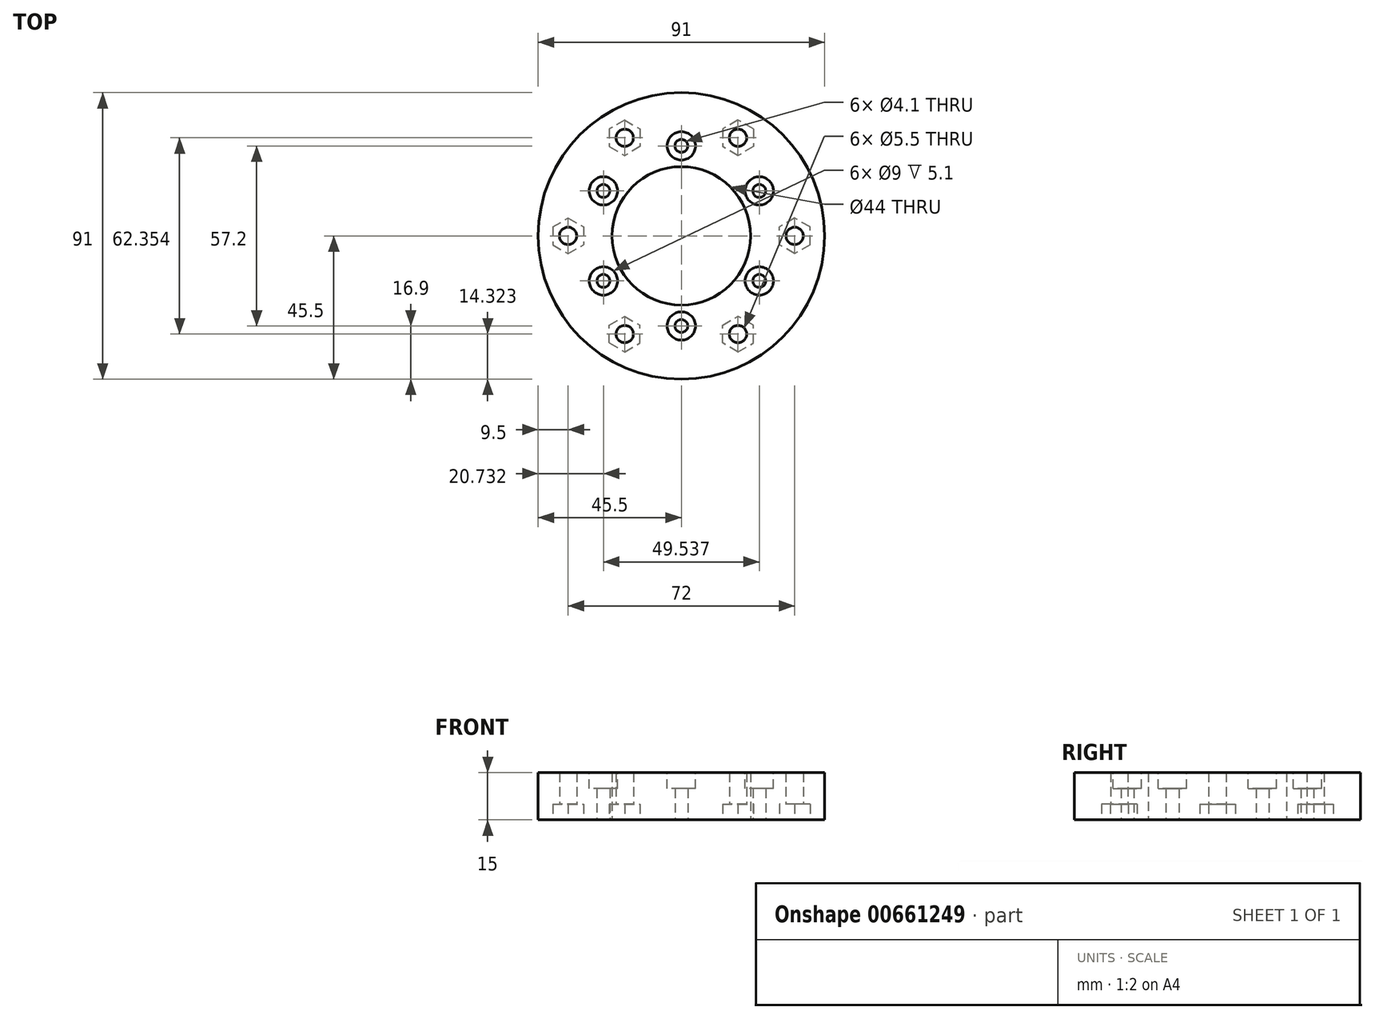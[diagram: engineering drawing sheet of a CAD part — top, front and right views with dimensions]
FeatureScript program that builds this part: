
annotation { "Feature Type Name" : "Feature", "Feature Type Description" : "" }
export const myFeature = defineFeature(function(context is Context, id is Id, definition is map)
    precondition{}
    {
        {
            var Q0;
            Q0=qCreatedBy(makeId("Top.planeOp"),FACE);
            var sketch = newSketch(context, id + "F0", { "sketchPlane" : qUnion([Q0])});
            skCircle(sketch, "E0", {"center": v(0, 0) * mm, "radius": 36 * mm, "construction": true});
            skCircle(sketch, "E1", {"center": v(18, 31.18) * mm, "radius": 2.75 * mm});
            skCircle(sketch, "E2", {"center": v(36, 0) * mm, "radius": 2.75 * mm});
            skCircle(sketch, "E3", {"center": v(-18, 31.18) * mm, "radius": 2.75 * mm});
            skCircle(sketch, "E4", {"center": v(-36, 0) * mm, "radius": 2.75 * mm});
            skCircle(sketch, "E5", {"center": v(-18, -31.18) * mm, "radius": 2.75 * mm});
            skCircle(sketch, "E6", {"center": v(18, -31.18) * mm, "radius": 2.75 * mm});
            skCircle(sketch, "E7", {"center": v(0, 0) * mm, "radius": 45.5 * mm});
            skCircle(sketch, "E8", {"center": v(0, 0) * mm, "radius": 28.6 * mm, "construction": true});
            skCircle(sketch, "E9", {"center": v(0, 28.6) * mm, "radius": 2.05 * mm});
            skCircle(sketch, "E10", {"center": v(24.77, 14.3) * mm, "radius": 2.05 * mm});
            skCircle(sketch, "E11", {"center": v(24.77, -14.3) * mm, "radius": 2.05 * mm});
            skCircle(sketch, "E12", {"center": v(0, -28.6) * mm, "radius": 2.05 * mm});
            skCircle(sketch, "E13", {"center": v(-24.77, -14.3) * mm, "radius": 2.05 * mm});
            skCircle(sketch, "E14", {"center": v(-24.77, 14.3) * mm, "radius": 2.05 * mm});
            skCircle(sketch, "E15", {"center": v(0, 0) * mm, "radius": 22 * mm});
            skCircle(sketch, "E16", {"center": v(-18, -31.18) * mm, "radius": 5.65 * mm, "construction": true});
            skLineSegment(sketch, "E17", {"start": v(-18, -31.18) * mm, "end": v(-18, -25.53) * mm, "construction": true});
            skLineSegment(sketch, "E18", {"start": v(-18, -25.53) * mm, "end": v(-13.1, -28.35) * mm});
            skLineSegment(sketch, "E19", {"start": v(-13.1, -28.35) * mm, "end": v(-18, -31.18) * mm, "construction": true});
            skLineSegment(sketch, "E20", {"start": v(-18, -31.18) * mm, "end": v(-13.1, -34) * mm, "construction": true});
            skLineSegment(sketch, "E21", {"start": v(-13.1, -34) * mm, "end": v(-13.1, -28.35) * mm});
            skLineSegment(sketch, "E22", {"start": v(-18, -31.18) * mm, "end": v(-18, -36.83) * mm, "construction": true});
            skLineSegment(sketch, "E23", {"start": v(-18, -36.83) * mm, "end": v(-13.1, -34) * mm});
            skLineSegment(sketch, "E24", {"start": v(-18, -31.18) * mm, "end": v(-22.9, -34) * mm, "construction": true});
            skLineSegment(sketch, "E25", {"start": v(-22.9, -34) * mm, "end": v(-18, -36.83) * mm});
            skLineSegment(sketch, "E26", {"start": v(-22.9, -34) * mm, "end": v(-22.9, -28.35) * mm});
            skLineSegment(sketch, "E27", {"start": v(-22.9, -28.35) * mm, "end": v(-18, -31.18) * mm, "construction": true});
            skLineSegment(sketch, "E28", {"start": v(-22.9, -28.35) * mm, "end": v(-18, -25.53) * mm});
            skLineSegment(sketch, "E29.1.0", {"start": v(13.1, -28.35) * mm, "end": v(18, -25.53) * mm});
            skLineSegment(sketch, "E29.1.1", {"start": v(22.9, -28.35) * mm, "end": v(18, -25.53) * mm});
            skLineSegment(sketch, "E29.1.2", {"start": v(22.9, -34) * mm, "end": v(22.9, -28.35) * mm});
            skLineSegment(sketch, "E29.1.3", {"start": v(18, -36.83) * mm, "end": v(22.9, -34) * mm});
            skLineSegment(sketch, "E29.1.4", {"start": v(18, -36.83) * mm, "end": v(13.1, -34) * mm});
            skLineSegment(sketch, "E29.1.5", {"start": v(13.1, -34) * mm, "end": v(13.1, -28.35) * mm});
            skLineSegment(sketch, "E29.2.0", {"start": v(31.1, -2.82) * mm, "end": v(31.1, 2.83) * mm});
            skLineSegment(sketch, "E29.2.1", {"start": v(36, 5.65) * mm, "end": v(31.1, 2.83) * mm});
            skLineSegment(sketch, "E29.2.2", {"start": v(40.9, 2.83) * mm, "end": v(36, 5.65) * mm});
            skLineSegment(sketch, "E29.2.3", {"start": v(40.9, -2.82) * mm, "end": v(40.9, 2.83) * mm});
            skLineSegment(sketch, "E29.2.4", {"start": v(40.9, -2.82) * mm, "end": v(36, -5.65) * mm});
            skLineSegment(sketch, "E29.2.5", {"start": v(36, -5.65) * mm, "end": v(31.1, -2.82) * mm});
            skLineSegment(sketch, "E29.3.0", {"start": v(18, 25.53) * mm, "end": v(13.1, 28.35) * mm});
            skLineSegment(sketch, "E29.3.1", {"start": v(13.1, 34) * mm, "end": v(13.1, 28.35) * mm});
            skLineSegment(sketch, "E29.3.2", {"start": v(18, 36.83) * mm, "end": v(13.1, 34) * mm});
            skLineSegment(sketch, "E29.3.3", {"start": v(22.9, 34) * mm, "end": v(18, 36.83) * mm});
            skLineSegment(sketch, "E29.3.4", {"start": v(22.9, 34) * mm, "end": v(22.9, 28.35) * mm});
            skLineSegment(sketch, "E29.3.5", {"start": v(22.9, 28.35) * mm, "end": v(18, 25.53) * mm});
            skLineSegment(sketch, "E29.4.0", {"start": v(-13.1, 28.35) * mm, "end": v(-18, 25.53) * mm});
            skLineSegment(sketch, "E29.4.1", {"start": v(-22.9, 28.35) * mm, "end": v(-18, 25.53) * mm});
            skLineSegment(sketch, "E29.4.2", {"start": v(-22.9, 34) * mm, "end": v(-22.9, 28.35) * mm});
            skLineSegment(sketch, "E29.4.3", {"start": v(-18, 36.83) * mm, "end": v(-22.9, 34) * mm});
            skLineSegment(sketch, "E29.4.4", {"start": v(-18, 36.83) * mm, "end": v(-13.1, 34) * mm});
            skLineSegment(sketch, "E29.4.5", {"start": v(-13.1, 34) * mm, "end": v(-13.1, 28.35) * mm});
            skLineSegment(sketch, "E29.5.0", {"start": v(-31.1, 2.82) * mm, "end": v(-31.1, -2.83) * mm});
            skLineSegment(sketch, "E29.5.1", {"start": v(-36, -5.65) * mm, "end": v(-31.1, -2.83) * mm});
            skLineSegment(sketch, "E29.5.2", {"start": v(-40.9, -2.83) * mm, "end": v(-36, -5.65) * mm});
            skLineSegment(sketch, "E29.5.3", {"start": v(-40.9, 2.82) * mm, "end": v(-40.9, -2.83) * mm});
            skLineSegment(sketch, "E29.5.4", {"start": v(-40.9, 2.82) * mm, "end": v(-36, 5.65) * mm});
            skLineSegment(sketch, "E29.5.5", {"start": v(-36, 5.65) * mm, "end": v(-31.1, 2.82) * mm});
            skSolve(sketch);
        }
        {
            var Q0;
            Q0=makeQuery(id+"F0.imprint","IMPRINT",FACE,{"disambiguationData":[TD([[makeQuery(id+"F0.imprint","IMPRINT",EDGE,{"derivedFrom":sQuery(id+"F0.wireOp",EDGE,"E7")}),1.0]])]});
            var Q1;
            Q1=makeQuery(id+"F0.imprint","IMPRINT",FACE,{"disambiguationData":[TD([[makeQuery(id+"F0.imprint","IMPRINT",EDGE,{"derivedFrom":sQuery(id+"F0.wireOp",EDGE,"E4")}),-1.0]])]});
            var Q2;
            Q2=makeQuery(id+"F0.imprint","IMPRINT",FACE,{"disambiguationData":[TD([[makeQuery(id+"F0.imprint","IMPRINT",EDGE,{"derivedFrom":sQuery(id+"F0.wireOp",EDGE,"E5")}),-1.0]])]});
            var Q3;
            Q3=makeQuery(id+"F0.imprint","IMPRINT",FACE,{"disambiguationData":[TD([[makeQuery(id+"F0.imprint","IMPRINT",EDGE,{"derivedFrom":sQuery(id+"F0.wireOp",EDGE,"E6")}),-1.0]])]});
            var Q4;
            Q4=makeQuery(id+"F0.imprint","IMPRINT",FACE,{"disambiguationData":[TD([[makeQuery(id+"F0.imprint","IMPRINT",EDGE,{"derivedFrom":sQuery(id+"F0.wireOp",EDGE,"E2")}),-1.0]])]});
            var Q5;
            Q5=makeQuery(id+"F0.imprint","IMPRINT",FACE,{"disambiguationData":[TD([[makeQuery(id+"F0.imprint","IMPRINT",EDGE,{"derivedFrom":sQuery(id+"F0.wireOp",EDGE,"E1")}),-1.0]])]});
            var Q6;
            Q6=makeQuery(id+"F0.imprint","IMPRINT",FACE,{"disambiguationData":[TD([[makeQuery(id+"F0.imprint","IMPRINT",EDGE,{"derivedFrom":sQuery(id+"F0.wireOp",EDGE,"E3")}),-1.0]])]});
            extrude(context, id + "F1", {"entities" : qUnion([Q0, Q1, Q2, Q3, Q4, Q5, Q6]), "depth" : 15 * mm, "offsetDistance" : 25 * mm});
        }
        {
            var Q0;
            Q0=makeQuery(id+"F1.opExtrude","CAP_FACE",FACE,{"disambiguationData":[OSD([sQuery(id+"F0.wireOp",EDGE,"E1"),sQuery(id+"F0.wireOp",EDGE,"E2"),sQuery(id+"F0.wireOp",EDGE,"E3"),sQuery(id+"F0.wireOp",EDGE,"E4"),sQuery(id+"F0.wireOp",EDGE,"E5"),sQuery(id+"F0.wireOp",EDGE,"E6"),sQuery(id+"F0.wireOp",EDGE,"E7"),sQuery(id+"F0.wireOp",EDGE,"E9"),sQuery(id+"F0.wireOp",EDGE,"E10"),sQuery(id+"F0.wireOp",EDGE,"E11"),sQuery(id+"F0.wireOp",EDGE,"E12"),sQuery(id+"F0.wireOp",EDGE,"E13"),sQuery(id+"F0.wireOp",EDGE,"E14"),sQuery(id+"F0.wireOp",EDGE,"E15")])],"isStart":false});
            var sketch = newSketch(context, id + "F2", { "sketchPlane" : qUnion([Q0])});
            skCircle(sketch, "E30", {"center": v(-24.77, -14.3) * mm, "radius": 4.5 * mm});
            skCircle(sketch, "E31", {"center": v(-24.77, 14.3) * mm, "radius": 4.5 * mm});
            skCircle(sketch, "E32", {"center": v(0, 28.6) * mm, "radius": 4.5 * mm});
            skCircle(sketch, "E33", {"center": v(24.77, 14.3) * mm, "radius": 4.5 * mm});
            skCircle(sketch, "E34", {"center": v(24.77, -14.3) * mm, "radius": 4.5 * mm});
            skCircle(sketch, "E35", {"center": v(0, -28.6) * mm, "radius": 4.5 * mm});
            skSolve(sketch);
        }
        {
            var Q0;
            Q0=makeQuery(id+"F2.imprint","IMPRINT",FACE,{"disambiguationData":[TD([[makeQuery(id+"F2.imprint","IMPRINT",EDGE,{"derivedFrom":sQuery(id+"F2.wireOp",EDGE,"E33")}),1.0]])]});
            var Q1;
            Q1=makeQuery(id+"F2.imprint","IMPRINT",FACE,{"disambiguationData":[TD([[makeQuery(id+"F2.imprint","IMPRINT",EDGE,{"derivedFrom":sQuery(id+"F2.wireOp",EDGE,"E31")}),1.0]])]});
            var Q2;
            Q2=makeQuery(id+"F2.imprint","IMPRINT",FACE,{"disambiguationData":[TD([[makeQuery(id+"F2.imprint","IMPRINT",EDGE,{"derivedFrom":sQuery(id+"F2.wireOp",EDGE,"E32")}),1.0]])]});
            var Q3;
            Q3=makeQuery(id+"F2.imprint","IMPRINT",FACE,{"disambiguationData":[TD([[makeQuery(id+"F2.imprint","IMPRINT",EDGE,{"derivedFrom":sQuery(id+"F2.wireOp",EDGE,"E30")}),1.0]])]});
            var Q4;
            Q4=makeQuery(id+"F2.imprint","IMPRINT",FACE,{"disambiguationData":[TD([[makeQuery(id+"F2.imprint","IMPRINT",EDGE,{"derivedFrom":sQuery(id+"F2.wireOp",EDGE,"E35")}),1.0]])]});
            var Q5;
            Q5=makeQuery(id+"F2.imprint","IMPRINT",FACE,{"disambiguationData":[TD([[makeQuery(id+"F2.imprint","IMPRINT",EDGE,{"derivedFrom":sQuery(id+"F2.wireOp",EDGE,"E34")}),1.0]])]});
            extrude(context, id + "F3", {"entities" : qUnion([Q0, Q1, Q2, Q3, Q4, Q5]), "operationType" : NewBodyOperationType.REMOVE, "oppositeDirection" : true, "depth" : 5.1 * mm, "offsetDistance" : 25 * mm});
        }
        {
            var Q0;
            Q0=makeQuery(id+"F0.imprint","IMPRINT",FACE,{"disambiguationData":[TD([[makeQuery(id+"F0.imprint","IMPRINT",EDGE,{"derivedFrom":sQuery(id+"F0.wireOp",EDGE,"E5")}),-1.0]])]});
            var Q1;
            Q1=makeQuery(id+"F0.imprint","IMPRINT",FACE,{"disambiguationData":[TD([[makeQuery(id+"F0.imprint","IMPRINT",EDGE,{"derivedFrom":sQuery(id+"F0.wireOp",EDGE,"E6")}),-1.0]])]});
            var Q2;
            Q2=makeQuery(id+"F0.imprint","IMPRINT",FACE,{"disambiguationData":[TD([[makeQuery(id+"F0.imprint","IMPRINT",EDGE,{"derivedFrom":sQuery(id+"F0.wireOp",EDGE,"E2")}),-1.0]])]});
            var Q3;
            Q3=makeQuery(id+"F0.imprint","IMPRINT",FACE,{"disambiguationData":[TD([[makeQuery(id+"F0.imprint","IMPRINT",EDGE,{"derivedFrom":sQuery(id+"F0.wireOp",EDGE,"E1")}),-1.0]])]});
            var Q4;
            Q4=makeQuery(id+"F0.imprint","IMPRINT",FACE,{"disambiguationData":[TD([[makeQuery(id+"F0.imprint","IMPRINT",EDGE,{"derivedFrom":sQuery(id+"F0.wireOp",EDGE,"E3")}),-1.0]])]});
            var Q5;
            Q5=makeQuery(id+"F0.imprint","IMPRINT",FACE,{"disambiguationData":[TD([[makeQuery(id+"F0.imprint","IMPRINT",EDGE,{"derivedFrom":sQuery(id+"F0.wireOp",EDGE,"E4")}),-1.0]])]});
            extrude(context, id + "F4", {"entities" : qUnion([Q0, Q1, Q2, Q3, Q4, Q5]), "operationType" : NewBodyOperationType.REMOVE, "depth" : 5 * mm, "offsetDistance" : 25 * mm});
        }
    });
